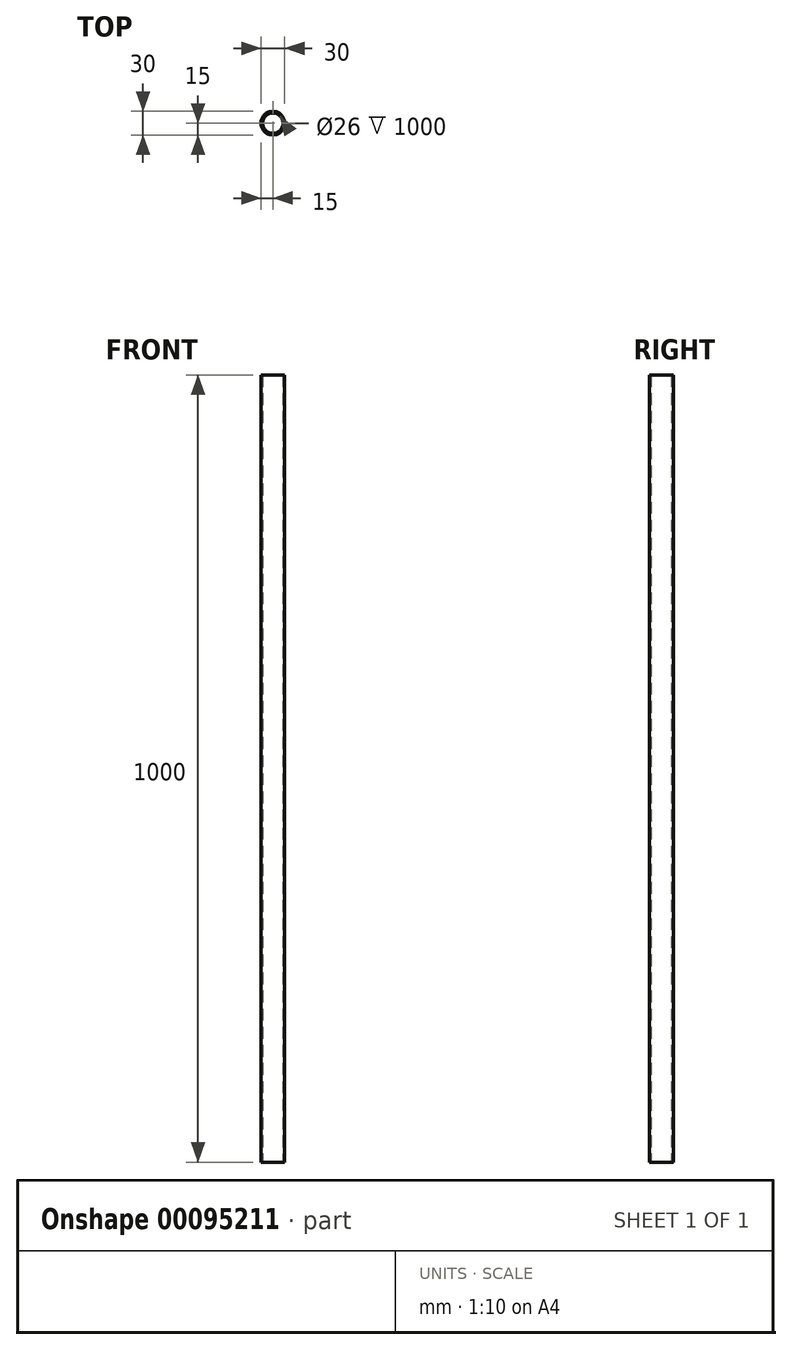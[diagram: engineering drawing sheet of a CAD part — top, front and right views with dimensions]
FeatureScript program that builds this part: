
annotation { "Feature Type Name" : "Feature", "Feature Type Description" : "" }
export const myFeature = defineFeature(function(context is Context, id is Id, definition is map)
    precondition{}
    {
        {
            var Q0;
            Q0=qCreatedBy(makeId("Top.planeOp"),FACE);
            var sketch = newSketch(context, id + "F0", { "sketchPlane" : qUnion([Q0])});
            skCircle(sketch, "E0", {"center": v(0, 0) * mm, "radius": 15 * mm});
            skCircle(sketch, "E1", {"center": v(0, 0) * mm, "radius": 13 * mm});
            skSolve(sketch);
        }
        {
            var Q0;
            Q0 = qSketchRegion(id + "F0", true);
            extrude(context, id + "F1", {"entities" : qUnion([Q0]), "depth" : 1000 * mm});
        }
    });
